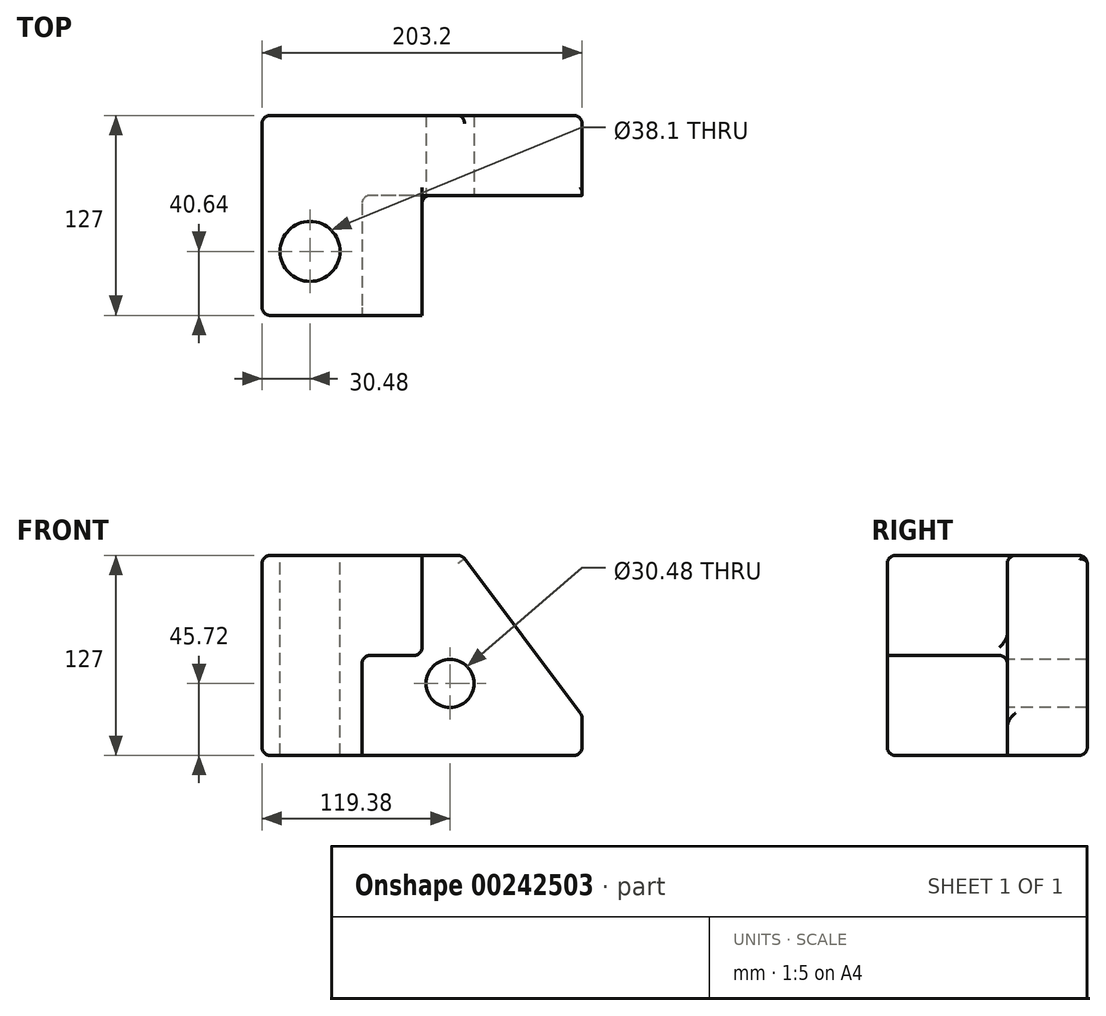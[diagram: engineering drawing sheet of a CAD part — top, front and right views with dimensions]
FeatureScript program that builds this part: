
annotation { "Feature Type Name" : "Feature", "Feature Type Description" : "" }
export const myFeature = defineFeature(function(context is Context, id is Id, definition is map)
    precondition{}
    {
        {
            var Q0;
            Q0=qCreatedBy(makeId("Front.planeOp"),FACE);
            var sketch = newSketch(context, id + "F0", { "sketchPlane" : qUnion([Q0])});
            skLineSegment(sketch, "E0.bottom", {"start": v(101.6, 63.5) * mm, "end": v(-101.6, 63.5) * mm});
            skLineSegment(sketch, "E0.top", {"start": v(101.6, -63.5) * mm, "end": v(-101.6, -63.5) * mm});
            skLineSegment(sketch, "E0.left", {"start": v(101.6, 63.5) * mm, "end": v(101.6, -63.5) * mm});
            skLineSegment(sketch, "E0.right", {"start": v(-101.6, 63.5) * mm, "end": v(-101.6, -63.5) * mm});
            skPoint(sketch, "E0.middle", {"position": v(0, 0) * mm});
            skPoint(sketch, "E1.start.orphan", {"position": v(0, 63.5) * mm});
            skSolve(sketch);
        }
        {
            var Q0;
            Q0 = qSketchRegion(id + "F0", true);
            extrude(context, id + "F1", {"entities" : qUnion([Q0]), "depth" : 127 * mm});
        }
        {
            var Q0;
            Q0=makeQuery(id+"F1.opExtrude","CAP_FACE",FACE,{"disambiguationData":[OSD([sQuery(id+"F0.wireOp",EDGE,"E0.bottom"),sQuery(id+"F0.wireOp",EDGE,"E0.top"),sQuery(id+"F0.wireOp",EDGE,"E0.left"),sQuery(id+"F0.wireOp",EDGE,"E0.right")])],"isStart":false});
            var sketch = newSketch(context, id + "F2", { "sketchPlane" : qUnion([Q0])});
            skLineSegment(sketch, "E2", {"start": v(-101.6, 63.5) * mm, "end": v(0, 63.5) * mm});
            skLineSegment(sketch, "E3", {"start": v(0, 63.5) * mm, "end": v(0, 0) * mm});
            skLineSegment(sketch, "E4", {"start": v(0, 0) * mm, "end": v(-38.1, 0) * mm});
            skLineSegment(sketch, "E5", {"start": v(-38.1, 0) * mm, "end": v(-38.1, -63.5) * mm});
            skLineSegment(sketch, "E6", {"start": v(-38.1, -63.5) * mm, "end": v(-101.6, -63.5) * mm});
            skLineSegment(sketch, "E7", {"start": v(-101.6, -63.5) * mm, "end": v(-101.6, 63.5) * mm});
            skSolve(sketch);
        }
        {
            var Q0;
            {var subQ2=sQuery(id+"F2.wireOp",EDGE,"E3");Q0=makeQuery(id+"F2.imprint","IMPRINT",FACE,{"disambiguationData":[TD([[makeQuery(id+"F2.imprint","IMPRINT",EDGE,{"derivedFrom":subQ2}),1.0]])]});}
            extrude(context, id + "F3", {"entities" : qUnion([Q0]), "operationType" : NewBodyOperationType.REMOVE, "oppositeDirection" : true, "depth" : 76.2 * mm});
        }
        {
            var Q0;
            Q0=makeQuery(id+"F1.opExtrude","SWEPT_EDGE",EDGE,{"disambiguationData":[OSD([sQuery(id+"F0.wireOp",EDGE,"E0.bottom"),sQuery(id+"F0.wireOp",EDGE,"E0.left")])]});
            chamfer(context, id + "F4", {"entities" : qUnion([Q0]), "chamferType" : ChamferType.TWO_OFFSETS, "width1" : 76.2 * mm, "oppositeDirection" : false, "width2" : 101.6 * mm, "tangentPropagation" : true});
        }
        {
            var Q0;
            {var subQ0=sQuery(id+"F0.wireOp",EDGE,"E0.bottom");Q0=makeQuery(id+"F4.opChamfer","BLEND_EDGE",EDGE,{"blendedFrom":[makeQuery(id+"F1.opExtrude","SWEPT_EDGE",EDGE,{"disambiguationData":[OSD([subQ0,sQuery(id+"F0.wireOp",EDGE,"E0.left")])]}),makeQuery(id+"F1.opExtrude","SWEPT_FACE",FACE,{"disambiguationData":[OSD([subQ0])]})],"blendedInto":[makeQuery(id+"F1.opExtrude","SWEPT_FACE",FACE,{"disambiguationData":[OSD([subQ0])]})]});}
            var Q1;
            Q1=makeQuery(id+"F3.boolean.opBoolean","COPY",EDGE,{"derivedFrom":makeQuery(id+"F3.opExtrude","SWEPT_EDGE",EDGE,{"disambiguationData":[OSD([sQuery(id+"F0.wireOp",EDGE,"E0.bottom"),sQuery(id+"F2.wireOp",EDGE,"E2"),sQuery(id+"F2.wireOp",EDGE,"E3")])]})});
            var Q2;
            Q2=makeQuery(id+"F3.boolean.opBoolean","COPY",EDGE,{"derivedFrom":makeQuery(id+"F3.opExtrude","CAP_EDGE",EDGE,{"disambiguationData":[OSD([sQuery(id+"F0.wireOp",EDGE,"E0.bottom")])],"isStart":false})});
            var Q3;
            Q3=makeQuery(id+"F1.opExtrude","SWEPT_EDGE",EDGE,{"disambiguationData":[OSD([sQuery(id+"F0.wireOp",EDGE,"E0.bottom"),sQuery(id+"F0.wireOp",EDGE,"E0.right")])]});
            var Q4;
            Q4=makeQuery(id+"F1.opExtrude","CAP_EDGE",EDGE,{"disambiguationData":[OSD([sQuery(id+"F0.wireOp",EDGE,"E0.right")])],"isStart":false});
            var Q5;
            Q5=makeQuery(id+"F3.boolean.opBoolean","COPY",EDGE,{"derivedFrom":makeQuery(id+"F3.opExtrude","CAP_EDGE",EDGE,{"disambiguationData":[OSD([sQuery(id+"F2.wireOp",EDGE,"E4")])],"isStart":true})});
            var Q6;
            Q6=makeQuery(id+"F3.boolean.opBoolean","COPY",EDGE,{"derivedFrom":makeQuery(id+"F3.opExtrude","CAP_EDGE",EDGE,{"disambiguationData":[OSD([sQuery(id+"F2.wireOp",EDGE,"E3")])],"isStart":true})});
            var Q7;
            Q7=makeQuery(id+"F3.boolean.opBoolean","COPY",EDGE,{"derivedFrom":makeQuery(id+"F3.opExtrude","SWEPT_EDGE",EDGE,{"disambiguationData":[OSD([sQuery(id+"F2.wireOp",EDGE,"E3"),sQuery(id+"F2.wireOp",EDGE,"E4")])]})});
            var Q8;
            Q8=makeQuery(id+"F3.boolean.opBoolean","COPY",EDGE,{"derivedFrom":makeQuery(id+"F3.opExtrude","CAP_EDGE",EDGE,{"disambiguationData":[OSD([sQuery(id+"F2.wireOp",EDGE,"E5")])],"isStart":true})});
            var Q9;
            Q9=makeQuery(id+"F3.boolean.opBoolean","COPY",EDGE,{"derivedFrom":makeQuery(id+"F3.opExtrude","SWEPT_EDGE",EDGE,{"disambiguationData":[OSD([sQuery(id+"F0.wireOp",EDGE,"E0.top"),sQuery(id+"F2.wireOp",EDGE,"E5"),sQuery(id+"F2.wireOp",EDGE,"E6")])]})});
            var Q10;
            Q10=makeQuery(id+"F1.opExtrude","CAP_EDGE",EDGE,{"disambiguationData":[OSD([sQuery(id+"F0.wireOp",EDGE,"E0.top")])],"isStart":false});
            var Q11;
            Q11=makeQuery(id+"F3.boolean.opBoolean","COPY",EDGE,{"derivedFrom":makeQuery(id+"F3.opExtrude","CAP_EDGE",EDGE,{"disambiguationData":[OSD([sQuery(id+"F0.wireOp",EDGE,"E0.top")])],"isStart":false})});
            var Q12;
            Q12=makeQuery(id+"F1.opExtrude","SWEPT_EDGE",EDGE,{"disambiguationData":[OSD([sQuery(id+"F0.wireOp",EDGE,"E0.top"),sQuery(id+"F0.wireOp",EDGE,"E0.left")])]});
            var Q13;
            Q13=makeQuery(id+"F1.opExtrude","CAP_EDGE",EDGE,{"disambiguationData":[OSD([sQuery(id+"F0.wireOp",EDGE,"E0.right")])],"isStart":true});
            var Q14;
            Q14=makeQuery(id+"F1.opExtrude","CAP_EDGE",EDGE,{"disambiguationData":[OSD([sQuery(id+"F0.wireOp",EDGE,"E0.bottom")])],"isStart":true});
            var Q15;
            Q15=makeQuery(id+"F1.opExtrude","CAP_EDGE",EDGE,{"disambiguationData":[OSD([sQuery(id+"F0.wireOp",EDGE,"E0.top")])],"isStart":true});
            var Q16;
            Q16=makeQuery(id+"F1.opExtrude","SWEPT_EDGE",EDGE,{"disambiguationData":[OSD([sQuery(id+"F0.wireOp",EDGE,"E0.top"),sQuery(id+"F0.wireOp",EDGE,"E0.right")])]});
            var Q17;
            Q17=makeQuery(id+"F1.opExtrude","CAP_EDGE",EDGE,{"disambiguationData":[OSD([sQuery(id+"F0.wireOp",EDGE,"E0.bottom")])],"isStart":false});
            var Q18;
            Q18=makeQuery(id+"F3.boolean.opBoolean","COPY",EDGE,{"derivedFrom":makeQuery(id+"F3.opExtrude","CAP_EDGE",EDGE,{"disambiguationData":[OSD([sQuery(id+"F2.wireOp",EDGE,"E5")])],"isStart":false})});
            var Q19;
            Q19=makeQuery(id+"F3.boolean.opBoolean","COPY",EDGE,{"derivedFrom":makeQuery(id+"F3.opExtrude","CAP_EDGE",EDGE,{"disambiguationData":[OSD([sQuery(id+"F2.wireOp",EDGE,"E4")])],"isStart":false})});
            var Q20;
            Q20=makeQuery(id+"F3.boolean.opBoolean","COPY",EDGE,{"derivedFrom":makeQuery(id+"F3.opExtrude","SWEPT_EDGE",EDGE,{"disambiguationData":[OSD([sQuery(id+"F2.wireOp",EDGE,"E4"),sQuery(id+"F2.wireOp",EDGE,"E5")])]})});
            fillet(context, id + "F5", {"entities" : qUnion([Q0, Q1, Q2, Q3, Q4, Q5, Q6, Q7, Q8, Q9, Q10, Q11, Q12, Q13, Q14, Q15, Q16, Q17, Q18, Q19, Q20]), "radius" : 5.08 * mm, "tangentPropagation" : true, "allowEdgeOverflow" : false});
        }
        {
            var Q0;
            Q0=makeQuery(id+"F3.boolean.opBoolean","COPY",FACE,{"derivedFrom":makeQuery(id+"F3.opExtrude","CAP_FACE",FACE,{"disambiguationData":[OSD([sQuery(id+"F0.wireOp",EDGE,"E0.bottom"),sQuery(id+"F0.wireOp",EDGE,"E0.top"),sQuery(id+"F0.wireOp",EDGE,"E0.left"),sQuery(id+"F2.wireOp",EDGE,"E3"),sQuery(id+"F2.wireOp",EDGE,"E4"),sQuery(id+"F2.wireOp",EDGE,"E5")])],"isStart":false})});
            var sketch = newSketch(context, id + "F6", { "sketchPlane" : qUnion([Q0])});
            skCircle(sketch, "E8", {"center": v(17.78, -17.78) * mm, "radius": 15.24 * mm});
            skSolve(sketch);
        }
        {
            var Q0;
            Q0=makeQuery(id+"F6.imprint","IMPRINT",FACE,{"disambiguationData":[TD([[makeQuery(id+"F6.imprint","IMPRINT",EDGE,{"derivedFrom":sQuery(id+"F6.wireOp",EDGE,"E8")}),1.0]])]});
            var Q1;
            Q1=makeQuery(id+"F1.opExtrude","CAP_FACE",FACE,{"disambiguationData":[OSD([sQuery(id+"F0.wireOp",EDGE,"E0.bottom"),sQuery(id+"F0.wireOp",EDGE,"E0.top"),sQuery(id+"F0.wireOp",EDGE,"E0.left"),sQuery(id+"F0.wireOp",EDGE,"E0.right")])],"isStart":true});
            extrude(context, id + "F7", {"entities" : qUnion([Q0]), "operationType" : NewBodyOperationType.REMOVE, "endBound" : BoundingType.UP_TO_SURFACE, "oppositeDirection" : true, "endBoundEntityFace" : qUnion([Q1]), "depth" : 25.4 * mm});
        }
        {
            var Q0;
            Q0=makeQuery(id+"F1.opExtrude","SWEPT_FACE",FACE,{"disambiguationData":[OSD([sQuery(id+"F0.wireOp",EDGE,"E0.bottom")])]});
            var sketch = newSketch(context, id + "F8", { "sketchPlane" : qUnion([Q0])});
            skCircle(sketch, "E9", {"center": v(-71.12, -86.36) * mm, "radius": 19.05 * mm});
            skSolve(sketch);
        }
        {
            var Q0;
            Q0=makeQuery(id+"F8.imprint","IMPRINT",FACE,{"disambiguationData":[TD([[makeQuery(id+"F8.imprint","IMPRINT",EDGE,{"derivedFrom":sQuery(id+"F8.wireOp",EDGE,"E9")}),1.0]])]});
            var Q1;
            Q1=makeQuery(id+"F1.opExtrude","SWEPT_FACE",FACE,{"disambiguationData":[OSD([sQuery(id+"F0.wireOp",EDGE,"E0.top")])]});
            extrude(context, id + "F9", {"entities" : qUnion([Q0]), "operationType" : NewBodyOperationType.REMOVE, "endBound" : BoundingType.UP_TO_SURFACE, "oppositeDirection" : true, "endBoundEntityFace" : qUnion([Q1]), "depth" : 25.4 * mm});
        }
        {
            var Q0;
            {var subQ0=sQuery(id+"F0.wireOp",EDGE,"E0.left");var subQ1=sQuery(id+"F0.wireOp",EDGE,"E0.bottom");Q0=makeQuery(id+"F4.opChamfer","BLEND_EDGE",EDGE,{"blendedFrom":[makeQuery(id+"F1.opExtrude","SWEPT_EDGE",EDGE,{"disambiguationData":[OSD([subQ1,subQ0])]}),makeQuery(id+"F3.boolean.opBoolean","COPY",FACE,{"derivedFrom":makeQuery(id+"F3.opExtrude","CAP_FACE",FACE,{"disambiguationData":[OSD([subQ1,sQuery(id+"F0.wireOp",EDGE,"E0.top"),subQ0,sQuery(id+"F2.wireOp",EDGE,"E3"),sQuery(id+"F2.wireOp",EDGE,"E4"),sQuery(id+"F2.wireOp",EDGE,"E5")])],"isStart":false})})],"blendedInto":[makeQuery(id+"F3.boolean.opBoolean","COPY",FACE,{"derivedFrom":makeQuery(id+"F3.opExtrude","CAP_FACE",FACE,{"disambiguationData":[OSD([subQ1,sQuery(id+"F0.wireOp",EDGE,"E0.top"),subQ0,sQuery(id+"F2.wireOp",EDGE,"E3"),sQuery(id+"F2.wireOp",EDGE,"E4"),sQuery(id+"F2.wireOp",EDGE,"E5")])],"isStart":false})})]});}
            var Q1;
            {var subQ0=sQuery(id+"F0.wireOp",EDGE,"E0.left");Q1=makeQuery(id+"F4.opChamfer","BLEND_EDGE",EDGE,{"blendedFrom":[makeQuery(id+"F1.opExtrude","SWEPT_EDGE",EDGE,{"disambiguationData":[OSD([sQuery(id+"F0.wireOp",EDGE,"E0.bottom"),subQ0])]}),makeQuery(id+"F1.opExtrude","SWEPT_FACE",FACE,{"disambiguationData":[OSD([subQ0])]})],"blendedInto":[makeQuery(id+"F1.opExtrude","SWEPT_FACE",FACE,{"disambiguationData":[OSD([subQ0])]})]});}
            var Q2;
            Q2=makeQuery(id+"F1.opExtrude","CAP_EDGE",EDGE,{"disambiguationData":[OSD([sQuery(id+"F0.wireOp",EDGE,"E0.left")])],"isStart":true});
            var Q3;
            {var subQ0=sQuery(id+"F0.wireOp",EDGE,"E0.left");var subQ1=sQuery(id+"F0.wireOp",EDGE,"E0.bottom");Q3=makeQuery(id+"F4.opChamfer","BLEND_EDGE",EDGE,{"blendedFrom":[makeQuery(id+"F1.opExtrude","SWEPT_EDGE",EDGE,{"disambiguationData":[OSD([subQ1,subQ0])]}),makeQuery(id+"F1.opExtrude","CAP_FACE",FACE,{"disambiguationData":[OSD([subQ1,sQuery(id+"F0.wireOp",EDGE,"E0.top"),subQ0,sQuery(id+"F0.wireOp",EDGE,"E0.right")])],"isStart":true})],"blendedInto":[makeQuery(id+"F1.opExtrude","CAP_FACE",FACE,{"disambiguationData":[OSD([subQ1,sQuery(id+"F0.wireOp",EDGE,"E0.top"),subQ0,sQuery(id+"F0.wireOp",EDGE,"E0.right")])],"isStart":true})]});}
            fillet(context, id + "F10", {"entities" : qUnion([Q0, Q1, Q2, Q3]), "radius" : 5.08 * mm, "tangentPropagation" : true, "allowEdgeOverflow" : false});
        }
    });
